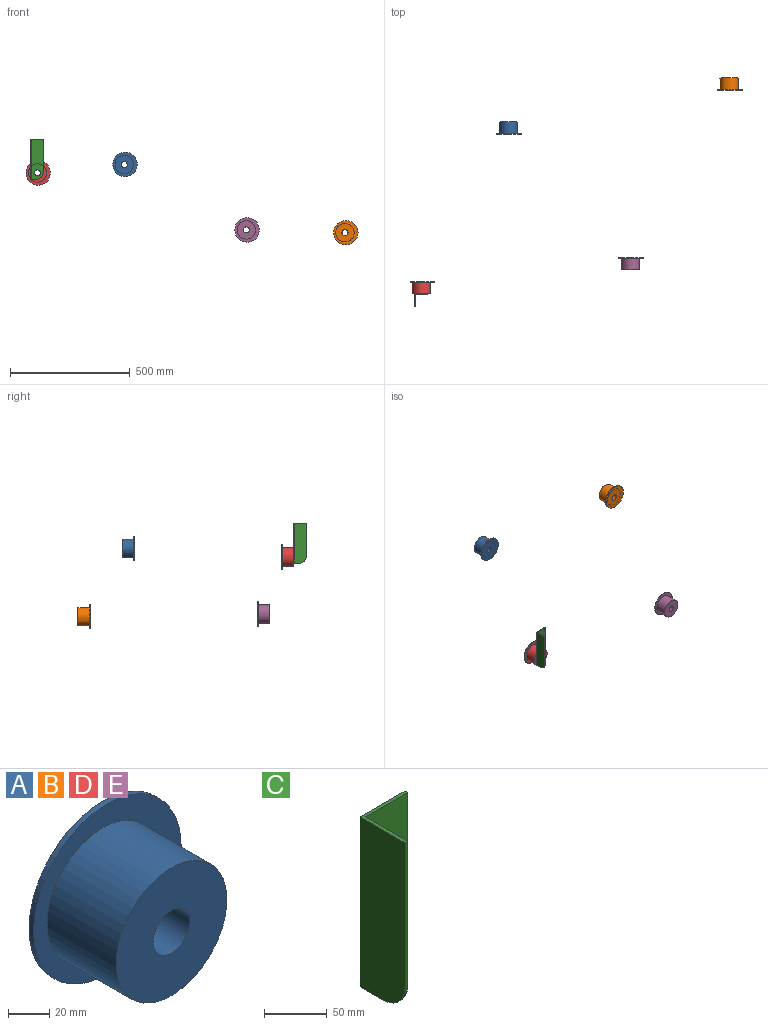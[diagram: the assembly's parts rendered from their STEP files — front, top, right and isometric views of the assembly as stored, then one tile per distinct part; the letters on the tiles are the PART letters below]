
ASSEMBLY  parts=5 mates=1
PART A: 6 faces, bbox 101.6x50.8x101.6 mm
  f0: cylinder r=38.1mm len=76.2mm, axis (0,1,0), area 11400.9mm2, adj f1,f4
  f1: plane 76.2x76.2mm, normal (0,-1,0), area 4053.7mm2, adj f0,f5
  f2: cylinder r=50.8mm len=101.6mm, axis (0,-1,0), area 1013.4mm2, adj f3,f4
  f3: plane 101.6x101.6mm, normal (0,1,0), area 7600.6mm2, adj f2,f5
  f4: plane 101.6x101.6mm, normal (0,-1,0), area 3547mm2, adj f0,f2
  f5: cylinder r=12.7mm len=50.8mm, axis (0,1,0), area 4053.7mm2, adj f1,f3
PART B: same geometry as A
PART C: 11 faces, bbox 50.8x50.8x166.6 mm
  f0: plane 50.8x50.8mm, normal (0,0,1), area 312.5mm2, adj f1,f3,f4,f5,f6,f7
  f1: plane 141.22x3.18mm, normal (1,0,0), area 448.4mm2, adj f0,f5,f7,f9
  f2: plane 25.4x25.4mm, normal (0,0,-1), area 151.2mm2, adj f3,f5,f6,f7,f9,f10
  f3: plane 166.62x50.8mm, normal (-1,0,0), area 8325.7mm2, adj f0,f2,f4,f5,f10
  f4: plane 141.22x3.18mm, normal (0,-1,0), area 448.4mm2, adj f0,f3,f6,f10
  f5: plane 166.62x50.8mm, normal (0,1,0), area 7819mm2, adj f0,f1,f2,f3,f8,f9
  f6: plane 166.62x47.63mm, normal (1,0,0), area 7796.7mm2, adj f0,f2,f4,f7,f10
  f7: plane 166.62x47.63mm, normal (0,-1,0), area 7290mm2, adj f0,f1,f2,f6,f8,f9
  f8: cylinder r=12.7mm len=25.4mm, axis (0,1,0), area 253.4mm2, adj f5,f7
  f9: cylinder r=25.4mm len=25.4mm, axis (0,-1,0), area 126.7mm2, adj f1,f2,f5,f7
  f10: cylinder r=25.4mm len=25.4mm, axis (-1,0,0), area 126.7mm2, adj f2,f3,f4,f6
PART D: same geometry as A
PART E: same geometry as A
PLACE A rot(axis=(-1,0,0),180deg) t=(-6.58,332.99,-32.04)mm
PLACE B rot(axis=(-1,0,0),180deg) t=(913.2,516.85,-316.43)mm
PLACE C t=(-346.98,-335.33,-34.95)mm
PLACE D t=(-368.87,-287.71,-67.4)mm
PLACE E t=(501.71,-187.33,-304.73)mm
MATE fastened C.f8 <-> D.f0  axis (0,1,0) through (-368.87,-335.33,-67.4)mm
